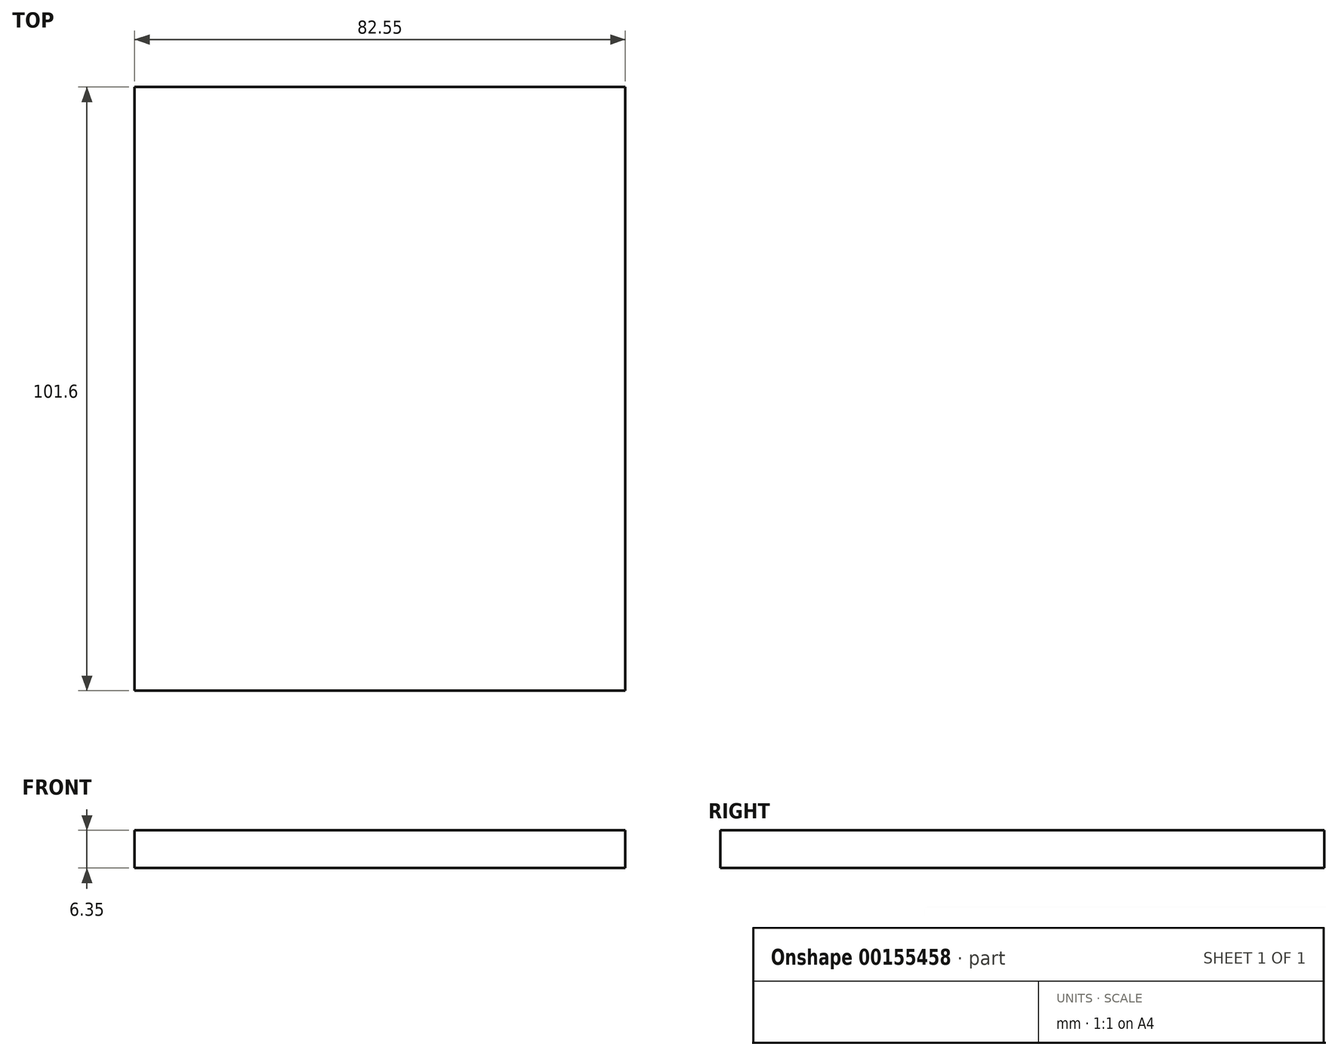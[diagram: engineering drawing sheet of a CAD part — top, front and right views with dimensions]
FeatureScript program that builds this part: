
annotation { "Feature Type Name" : "Feature", "Feature Type Description" : "" }
export const myFeature = defineFeature(function(context is Context, id is Id, definition is map)
    precondition{}
    {
        {
            var Q0;
            Q0=qCreatedBy(makeId("Top.planeOp"),FACE);
            var sketch = newSketch(context, id + "F0", { "sketchPlane" : qUnion([Q0])});
            skLineSegment(sketch, "E0.bottom", {"start": v(0, 0) * mm, "end": v(82.55, 0) * mm});
            skLineSegment(sketch, "E0.top", {"start": v(0, 101.6) * mm, "end": v(82.55, 101.6) * mm});
            skLineSegment(sketch, "E0.left", {"start": v(0, 0) * mm, "end": v(0, 101.6) * mm});
            skLineSegment(sketch, "E0.right", {"start": v(82.55, 0) * mm, "end": v(82.55, 101.6) * mm});
            skSolve(sketch);
        }
        {
            var Q0;
            Q0 = qSketchRegion(id + "F0", true);
            extrude(context, id + "F1", {"entities" : qUnion([Q0]), "depth" : 6.35 * mm});
        }
    });
